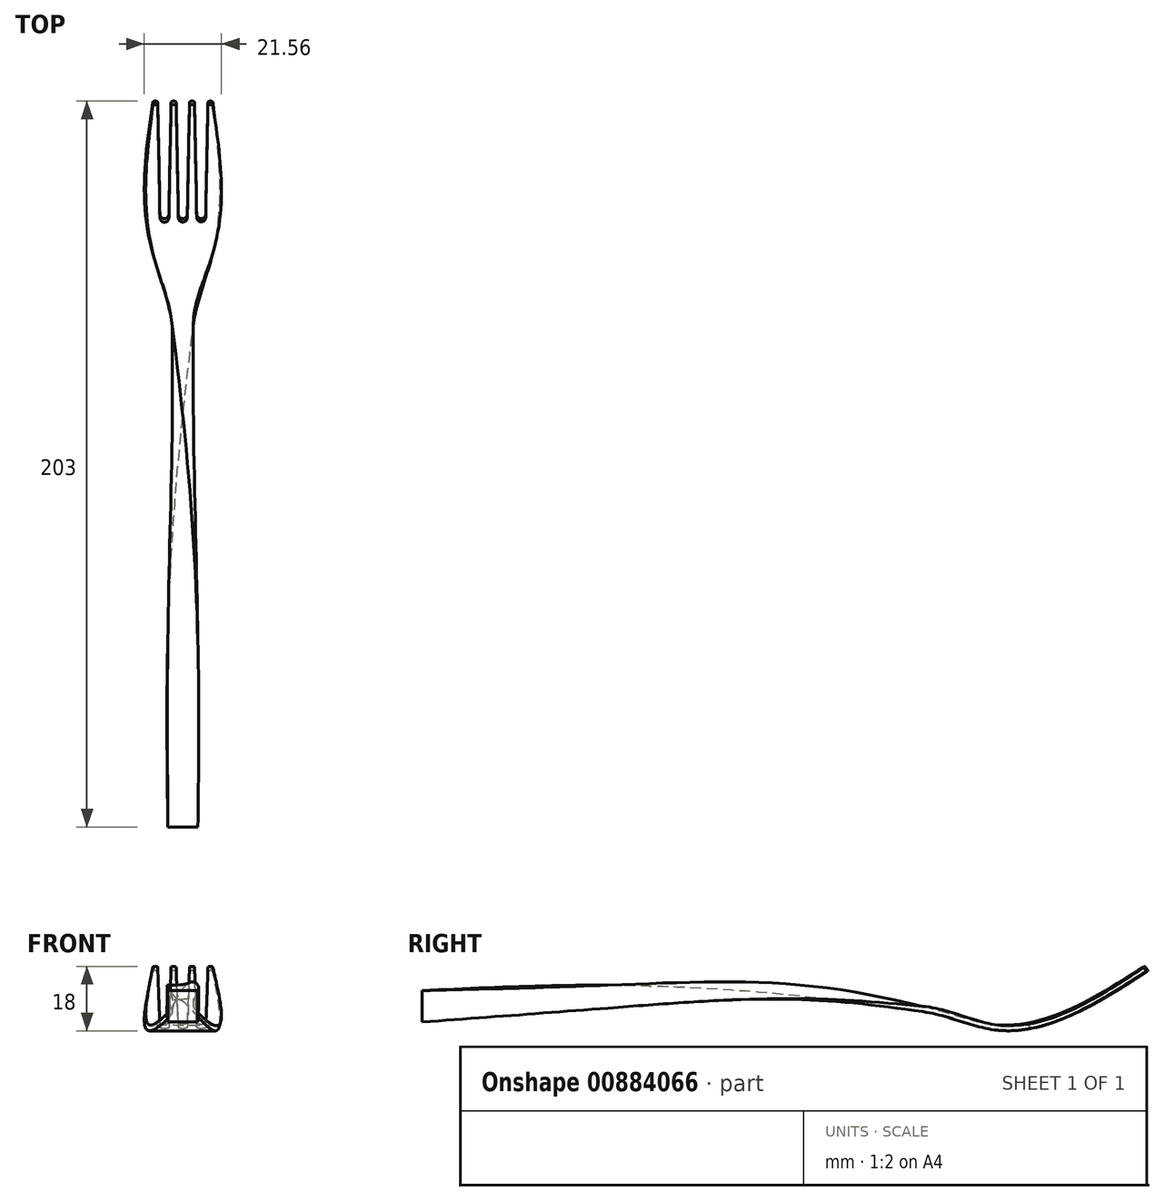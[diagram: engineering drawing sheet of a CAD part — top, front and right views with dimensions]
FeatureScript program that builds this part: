
annotation { "Feature Type Name" : "Feature", "Feature Type Description" : "" }
export const myFeature = defineFeature(function(context is Context, id is Id, definition is map)
    precondition{}
    {
        {
            var Q0;
            Q0=qCreatedBy(makeId("Front.planeOp"),FACE);
            var sketch = newSketch(context, id + "F0", { "sketchPlane" : qUnion([Q0])});
            skLineSegment(sketch, "E0.bottom", {"start": v(4.2, 4.4) * mm, "end": v(-4.2, 4.4) * mm});
            skLineSegment(sketch, "E0.top", {"start": v(4.2, -4.4) * mm, "end": v(-4.2, -4.4) * mm});
            skLineSegment(sketch, "E0.left", {"start": v(4.2, 4.4) * mm, "end": v(4.2, -4.4) * mm});
            skLineSegment(sketch, "E0.right", {"start": v(-4.2, 4.4) * mm, "end": v(-4.2, -4.4) * mm});
            skPoint(sketch, "E0.middle", {"position": v(0, 0) * mm});
            skSolve(sketch);
        }
        {
            var Q0;
            Q0=qCreatedBy(makeId("Front.planeOp"),FACE);
            cPlane(context, id + "F1", {"entities" : qUnion([Q0]), "cplaneType" : CPlaneType.OFFSET, "offset" : 115 * mm, "oppositeDirection" : true, "width" : 150 * mm, "height" : 150 * mm});
        }
        {
            var Q0;
            Q0=qCreatedBy(makeId("Front.planeOp"),FACE);
            cPlane(context, id + "F2", {"entities" : qUnion([Q0]), "cplaneType" : CPlaneType.OFFSET, "offset" : 52 * mm, "oppositeDirection" : true, "width" : 150 * mm, "height" : 150 * mm});
        }
        {
            var Q0;
            Q0=qCreatedBy(id+"F2.planeOp",FACE);
            var sketch = newSketch(context, id + "F3", { "sketchPlane" : qUnion([Q0])});
            skLineSegment(sketch, "E1", {"start": v(4.2, -0.5) * mm, "end": v(-4.2, -0.5) * mm});
            skPoint(sketch, "E2.orphan", {"position": v(4.2, -4.4) * mm});
            skPoint(sketch, "E3.orphan", {"position": v(-4.2, -4.4) * mm});
            skLineSegment(sketch, "E4", {"start": v(4.2, -0.5) * mm, "end": v(4.2, 5.9) * mm});
            skLineSegment(sketch, "E5", {"start": v(4.2, 5.9) * mm, "end": v(-4.2, 5.9) * mm});
            skLineSegment(sketch, "E6", {"start": v(-4.2, 5.9) * mm, "end": v(-4.2, -0.5) * mm});
            skSolve(sketch);
        }
        {
            var Q0;
            Q0=qCreatedBy(id+"F1.planeOp",FACE);
            var sketch = newSketch(context, id + "F4", { "sketchPlane" : qUnion([Q0])});
            skLineSegment(sketch, "E7", {"start": v(-2.95, 1.9) * mm, "end": v(2.95, 1.9) * mm, "construction": true});
            skPoint(sketch, "E8", {"position": v(0, 1.9) * mm});
            skPoint(sketch, "E9", {"position": v(0, 4.9) * mm});
            skLineSegment(sketch, "E10", {"start": v(2.95, 1.9) * mm, "end": v(0, 4.9) * mm});
            skLineSegment(sketch, "E11", {"start": v(-2.95, 1.9) * mm, "end": v(0, 4.9) * mm});
            skLineSegment(sketch, "E12", {"start": v(-2.95, 1.9) * mm, "end": v(0, 1.4) * mm});
            skLineSegment(sketch, "E13", {"start": v(0, 1.4) * mm, "end": v(2.95, 1.9) * mm});
            skSolve(sketch);
        }
        {
            var Q0;
            Q0=qCreatedBy(id+"F1.planeOp",FACE);
            cPlane(context, id + "F5", {"entities" : qUnion([Q0]), "cplaneType" : CPlaneType.OFFSET, "offset" : 25 * mm, "oppositeDirection" : true, "width" : 150 * mm, "height" : 150 * mm});
        }
        {
            var Q0;
            Q0=qCreatedBy(id+"F5.planeOp",FACE);
            var sketch = newSketch(context, id + "F6", { "sketchPlane" : qUnion([Q0])});
            skLineSegment(sketch, "E14.bottom", {"start": v(-2.9, -1.5) * mm, "end": v(2.9, -1.5) * mm});
            skLineSegment(sketch, "E14.top", {"start": v(-2.9, 0) * mm, "end": v(2.9, 0) * mm});
            skLineSegment(sketch, "E14.left", {"start": v(-2.9, -1.5) * mm, "end": v(-2.9, 0) * mm});
            skLineSegment(sketch, "E14.right", {"start": v(2.9, -1.5) * mm, "end": v(2.9, 0) * mm});
            skPoint(sketch, "E15", {"position": v(0, -1.5) * mm});
            skSolve(sketch);
        }
        {
            var Q0;
            Q0=makeQuery(id+"F0.imprint","IMPRINT",FACE,{"disambiguationData":[TD([[makeQuery(id+"F0.imprint","IMPRINT",EDGE,{"derivedFrom":sQuery(id+"F0.wireOp",EDGE,"E0.bottom")}),1.0]])]});
            var Q1;
            Q1=makeQuery(id+"F3.imprint","IMPRINT",FACE,{"disambiguationData":[TD([[makeQuery(id+"F3.imprint","IMPRINT",EDGE,{"derivedFrom":sQuery(id+"F3.wireOp",EDGE,"E1")}),-1.0]])]});
            var Q2;
            Q2=makeQuery(id+"F4.imprint","IMPRINT",FACE,{"disambiguationData":[TD([[makeQuery(id+"F4.imprint","IMPRINT",EDGE,{"derivedFrom":sQuery(id+"F4.wireOp",EDGE,"E10")}),1.0]])]});
            var Q3;
            Q3=makeQuery(id+"F6.imprint","IMPRINT",FACE,{"disambiguationData":[TD([[makeQuery(id+"F6.imprint","IMPRINT",EDGE,{"derivedFrom":sQuery(id+"F6.wireOp",EDGE,"E14.bottom")}),1.0]])]});
            var Q4;
            Q4=sQuery(id+"FWTZiSJ4yrXkOPS_0.wireOp",EDGE,"hAyMuFoN-GUzl-rf4k-sucj-0QNI1hfmMDkl");
            var Q5;
            Q5=sQuery(id+"FWTZiSJ4yrXkOPS_0.wireOp",EDGE,"t523Q2hn-vSHs-sRLZ-ii0p-p9g3PGXzJ7zO");
            var Q6;
            Q6=sQuery(id+"F0.wireOp",VERTEX,"E0.bottom.start");
            var Q7;
            Q7=sQuery(id+"F3.wireOp",VERTEX,"E4.end");
            var Q8;
            Q8=sQuery(id+"F4.wireOp",VERTEX,"E9");
            var Q9;
            Q9=sQuery(id+"F6.wireOp",VERTEX,"E14.top.start");
            loft(context, id + "F7", {"sheetProfilesArray" : [{ "sheetProfileEntities" : qUnion([Q0]) }, { "sheetProfileEntities" : qUnion([Q1]) }, { "sheetProfileEntities" : qUnion([Q2]) }, { "sheetProfileEntities" : qUnion([Q3]) }], "guidesArray" : [{ "guideEntities" : qUnion([Q4]), "guideDerivativeType" : LoftGuideDerivativeType.DEFAULT, "guideDerivativeMagnitude" : 1 }, { "guideEntities" : qUnion([Q5]), "guideDerivativeType" : LoftGuideDerivativeType.DEFAULT, "guideDerivativeMagnitude" : 1 }], "matchConnections" : true, "connections" : [{ "connectionEntities" : qUnion([Q6, Q7, Q8, Q9]), "connectionEdgeQueries" : qUnion([]), "connectionEdgeParameters" : [] }]});
        }
        {
            var Q0;
            Q0=qCreatedBy(makeId("Right.planeOp"),FACE);
            var sketch = newSketch(context, id + "F8", { "sketchPlane" : qUnion([Q0])});
            skFitSpline(sketch, "E16", {"points": [v(140, -1.5) * mm, v(150.94, -3.71) * mm, v(160.02, -6.6) * mm, v(171.67, -6.79) * mm, v(179.83, -5.37) * mm, v(189.79, -0.72) * mm, v(196.32, 4.27) * mm, v(203, 10) * mm], "startDerivative": vector(53.15, -7.29) * mm, "endDerivative": vector(30.89, 35.93) * mm});
            skSolve(sketch);
        }
        {
            var Q0;
            Q0=qCreatedBy(id+"F5.planeOp",FACE);
            cPlane(context, id + "F9", {"entities" : qUnion([Q0]), "cplaneType" : CPlaneType.OFFSET, "offset" : 20 * mm, "oppositeDirection" : true, "width" : 150 * mm, "height" : 150 * mm});
        }
        {
            var Q0;
            Q0=qCreatedBy(makeId("Right.planeOp"),FACE);
            var sketch = newSketch(context, id + "F10", { "sketchPlane" : qUnion([Q0])});
            skLineSegment(sketch, "E17", {"start": v(203, 10) * mm, "end": v(196.32, 4.27) * mm});
            skSolve(sketch);
        }
        {
            var Q0;
            Q0=sQuery(id+"F10.wireOp",VERTEX,"E17.start");
            var Q1;
            Q1=sQuery(id+"F10.wireOp",EDGE,"E17");
            cPlane(context, id + "F11", {"entities" : qUnion([Q0, Q1]), "cplaneType" : CPlaneType.LINE_POINT, "offset" : 25 * mm, "width" : 150 * mm, "height" : 150 * mm});
        }
        {
            var Q0;
            Q0=qCreatedBy(id+"F9.planeOp",FACE);
            var sketch = newSketch(context, id + "F12", { "sketchPlane" : qUnion([Q0])});
            skLineSegment(sketch, "E18.bottom", {"start": v(8.25, -5.1) * mm, "end": v(-8.25, -5.1) * mm});
            skLineSegment(sketch, "E18.top", {"start": v(8.25, -6.6) * mm, "end": v(-8.25, -6.6) * mm});
            skLineSegment(sketch, "E18.left", {"start": v(8.25, -5.1) * mm, "end": v(8.25, -6.6) * mm});
            skLineSegment(sketch, "E18.right", {"start": v(-8.25, -5.1) * mm, "end": v(-8.25, -6.6) * mm});
            skSolve(sketch);
        }
        {
            var Q0;
            Q0=qCreatedBy(id+"F11.planeOp",FACE);
            var sketch = newSketch(context, id + "F13", { "sketchPlane" : qUnion([Q0])});
            skLineSegment(sketch, "E19.bottom", {"start": v(8.35, -123.04) * mm, "end": v(-8.35, -123.04) * mm});
            skLineSegment(sketch, "E19.top", {"start": v(8.35, -124.54) * mm, "end": v(-8.35, -124.54) * mm});
            skLineSegment(sketch, "E19.left", {"start": v(8.35, -123.04) * mm, "end": v(8.35, -124.54) * mm});
            skLineSegment(sketch, "E19.right", {"start": v(-8.35, -123.04) * mm, "end": v(-8.35, -124.54) * mm});
            skSolve(sketch);
        }
        {
            var Q1;
            Q1=makeQuery(id+"F7.opLoft","CAP_FACE",FACE,{"disambiguationData":[OSD([makeQuery(id+"F6.imprint","IMPRINT",FACE,{"disambiguationData":[TD([[makeQuery(id+"F6.imprint","IMPRINT",EDGE,{"derivedFrom":sQuery(id+"F6.wireOp",EDGE,"E14.bottom")}),1.0]])]})])],"isStart":true});
            var Q2;
            Q2=makeQuery(id+"F12.imprint","IMPRINT",FACE,{"disambiguationData":[TD([[makeQuery(id+"F12.imprint","IMPRINT",EDGE,{"derivedFrom":sQuery(id+"F12.wireOp",EDGE,"E18.bottom")}),1.0]])]});
            var Q3;
            Q3=makeQuery(id+"F13.imprint","IMPRINT",FACE,{"disambiguationData":[TD([[makeQuery(id+"F13.imprint","IMPRINT",EDGE,{"derivedFrom":sQuery(id+"F13.wireOp",EDGE,"E19.bottom")}),1.0]])]});
            loft(context, id + "F14", {"operationType" : NewBodyOperationType.ADD, "startCondition" : LoftEndDerivativeType.MATCH_TANGENT, "startMagnitude" : 1, "sheetProfilesArray" : [{ "sheetProfileEntities" : qUnion([Q1]) }, { "sheetProfileEntities" : qUnion([Q2]) }, { "sheetProfileEntities" : qUnion([Q3]) }]});
        }
        {
            var Q0;
            Q0=makeQuery(id+"F14.opLoft","MID_CAP_EDGE",EDGE,{"disambiguationData":[OSD([sQuery(id+"F13.wireOp",EDGE,"E19.bottom"),sQuery(id+"F13.wireOp",EDGE,"E19.left"),sQuery(id+"F13.wireOp",EDGE,"E19.right")])],"capPos":2.0});
            cPlane(context, id + "F15", {"entities" : qUnion([Q0]), "cplaneType" : CPlaneType.LINE_ANGLE, "offset" : 25 * mm, "angle" : 125 * degree, "oppositeDirection" : true, "width" : 150 * mm, "height" : 150 * mm});
        }
        {
            var Q0;
            Q0=qCreatedBy(id+"F15.planeOp",FACE);
            var sketch = newSketch(context, id + "F16", { "sketchPlane" : qUnion([Q0])});
            skLineSegment(sketch, "E20", {"start": v(-7.02, -172.02) * mm, "end": v(-3.28, -172.02) * mm});
            skLineSegment(sketch, "E21", {"start": v(-1.87, -172.02) * mm, "end": v(1.87, -172.02) * mm});
            skLineSegment(sketch, "E22", {"start": v(3.28, -172.02) * mm, "end": v(7.03, -172.02) * mm});
            skLineSegment(sketch, "E23", {"start": v(-7.02, -172.02) * mm, "end": v(-6.41, -137.02) * mm});
            skLineSegment(sketch, "E24", {"start": v(-3.28, -172.02) * mm, "end": v(-3.89, -137.02) * mm});
            skLineSegment(sketch, "E25", {"start": v(-1.87, -172.02) * mm, "end": v(-1.26, -137.02) * mm});
            skLineSegment(sketch, "E26", {"start": v(1.87, -172.02) * mm, "end": v(1.26, -137.02) * mm});
            skLineSegment(sketch, "E27", {"start": v(3.28, -172.02) * mm, "end": v(3.86, -137.02) * mm});
            skLineSegment(sketch, "E28", {"start": v(7.03, -172.02) * mm, "end": v(6.41, -137.02) * mm});
            skLineSegment(sketch, "E29", {"start": v(-3.89, -137.02) * mm, "end": v(-1.26, -137.02) * mm, "construction": true});
            skLineSegment(sketch, "E30", {"start": v(-2.58, -137.02) * mm, "end": v(-2.58, -172.02) * mm, "construction": true});
            skLineSegment(sketch, "E31", {"start": v(-3.28, -172.02) * mm, "end": v(-1.87, -172.02) * mm, "construction": true});
            skArc(sketch, "E32", {"start": v(-3.89, -137.02) * mm, "mid": v(-5.15, -135.78) * mm, "end": v(-6.41, -137.02) * mm});
            skArc(sketch, "E33", {"start": v(1.26, -137.02) * mm, "mid": v(0, -135.78) * mm, "end": v(-1.26, -137.02) * mm});
            skArc(sketch, "E34", {"start": v(6.41, -137.02) * mm, "mid": v(5.14, -135.77) * mm, "end": v(3.86, -137.02) * mm});
            skSolve(sketch);
        }
        {
            var Q0;
            Q0 = qSketchRegion(id + "F16", true);
            extrude(context, id + "F17", {"entities" : qUnion([Q0]), "operationType" : NewBodyOperationType.REMOVE, "endBound" : BoundingType.THROUGH_ALL, "oppositeDirection" : true, "depth" : 25 * mm, "offsetDistance" : 25 * mm, "hasSecondDirection" : true, "secondDirectionBound" : SecondDirectionBoundingType.THROUGH_ALL, "secondDirectionOppositeDirection" : false, "secondDirectionDepth" : 25 * mm});
        }
        {
            var Q0;
            Q0=makeQuery(id+"F17.boolean.opBoolean","INTERSECT",EDGE,{"derivedFrom":[makeQuery(id+"F14.opLoft","CAP_FACE",FACE,{"disambiguationData":[OSD([makeQuery(id+"F13.imprint","IMPRINT",FACE,{"disambiguationData":[TD([[makeQuery(id+"F13.imprint","IMPRINT",EDGE,{"derivedFrom":sQuery(id+"F13.wireOp",EDGE,"E19.bottom")}),1.0]])]})])],"isStart":true}),makeQuery(id+"F17.opExtrude","SWEPT_FACE",FACE,{"disambiguationData":[OSD([sQuery(id+"F16.wireOp",EDGE,"E23")])]})]});
            var Q1;
            Q1=makeQuery(id+"F17.boolean.opBoolean","INTERSECT",EDGE,{"derivedFrom":[makeQuery(id+"F14.opLoft","CAP_FACE",FACE,{"disambiguationData":[OSD([makeQuery(id+"F13.imprint","IMPRINT",FACE,{"disambiguationData":[TD([[makeQuery(id+"F13.imprint","IMPRINT",EDGE,{"derivedFrom":sQuery(id+"F13.wireOp",EDGE,"E19.bottom")}),1.0]])]})])],"isStart":true}),makeQuery(id+"F17.opExtrude","SWEPT_FACE",FACE,{"disambiguationData":[OSD([sQuery(id+"F16.wireOp",EDGE,"E24")])]})]});
            var Q2;
            Q2=makeQuery(id+"F17.boolean.opBoolean","INTERSECT",EDGE,{"derivedFrom":[makeQuery(id+"F14.opLoft","CAP_FACE",FACE,{"disambiguationData":[OSD([makeQuery(id+"F13.imprint","IMPRINT",FACE,{"disambiguationData":[TD([[makeQuery(id+"F13.imprint","IMPRINT",EDGE,{"derivedFrom":sQuery(id+"F13.wireOp",EDGE,"E19.bottom")}),1.0]])]})])],"isStart":true}),makeQuery(id+"F17.opExtrude","SWEPT_FACE",FACE,{"disambiguationData":[OSD([sQuery(id+"F16.wireOp",EDGE,"E25")])]})]});
            var Q3;
            Q3=makeQuery(id+"F17.boolean.opBoolean","INTERSECT",EDGE,{"derivedFrom":[makeQuery(id+"F14.opLoft","CAP_FACE",FACE,{"disambiguationData":[OSD([makeQuery(id+"F13.imprint","IMPRINT",FACE,{"disambiguationData":[TD([[makeQuery(id+"F13.imprint","IMPRINT",EDGE,{"derivedFrom":sQuery(id+"F13.wireOp",EDGE,"E19.bottom")}),1.0]])]})])],"isStart":true}),makeQuery(id+"F17.opExtrude","SWEPT_FACE",FACE,{"disambiguationData":[OSD([sQuery(id+"F16.wireOp",EDGE,"E26")])]})]});
            var Q4;
            Q4=makeQuery(id+"F17.boolean.opBoolean","INTERSECT",EDGE,{"derivedFrom":[makeQuery(id+"F14.opLoft","CAP_FACE",FACE,{"disambiguationData":[OSD([makeQuery(id+"F13.imprint","IMPRINT",FACE,{"disambiguationData":[TD([[makeQuery(id+"F13.imprint","IMPRINT",EDGE,{"derivedFrom":sQuery(id+"F13.wireOp",EDGE,"E19.bottom")}),1.0]])]})])],"isStart":true}),makeQuery(id+"F17.opExtrude","SWEPT_FACE",FACE,{"disambiguationData":[OSD([sQuery(id+"F16.wireOp",EDGE,"E27")])]})]});
            var Q5;
            Q5=makeQuery(id+"F17.boolean.opBoolean","INTERSECT",EDGE,{"derivedFrom":[makeQuery(id+"F14.opLoft","CAP_FACE",FACE,{"disambiguationData":[OSD([makeQuery(id+"F13.imprint","IMPRINT",FACE,{"disambiguationData":[TD([[makeQuery(id+"F13.imprint","IMPRINT",EDGE,{"derivedFrom":sQuery(id+"F13.wireOp",EDGE,"E19.bottom")}),1.0]])]})])],"isStart":true}),makeQuery(id+"F17.opExtrude","SWEPT_FACE",FACE,{"disambiguationData":[OSD([sQuery(id+"F16.wireOp",EDGE,"E28")])]})]});
            var Q6;
            Q6=makeQuery(id+"F14.opLoft","MID_CAP_EDGE",EDGE,{"disambiguationData":[OSD([sQuery(id+"F13.wireOp",EDGE,"E19.bottom"),sQuery(id+"F13.wireOp",EDGE,"E19.top"),sQuery(id+"F13.wireOp",EDGE,"E19.right")])],"capPos":2.0});
            var Q7;
            Q7=makeQuery(id+"F14.opLoft","MID_CAP_EDGE",EDGE,{"disambiguationData":[OSD([sQuery(id+"F13.wireOp",EDGE,"E19.bottom"),sQuery(id+"F13.wireOp",EDGE,"E19.top"),sQuery(id+"F13.wireOp",EDGE,"E19.left")])],"capPos":2.0});
            fillet(context, id + "F18", {"entities" : qUnion([Q0, Q1, Q2, Q3, Q4, Q5, Q6, Q7]), "radius" : .5 * mm, "tangentPropagation" : true, "allowEdgeOverflow" : false});
        }
    });
